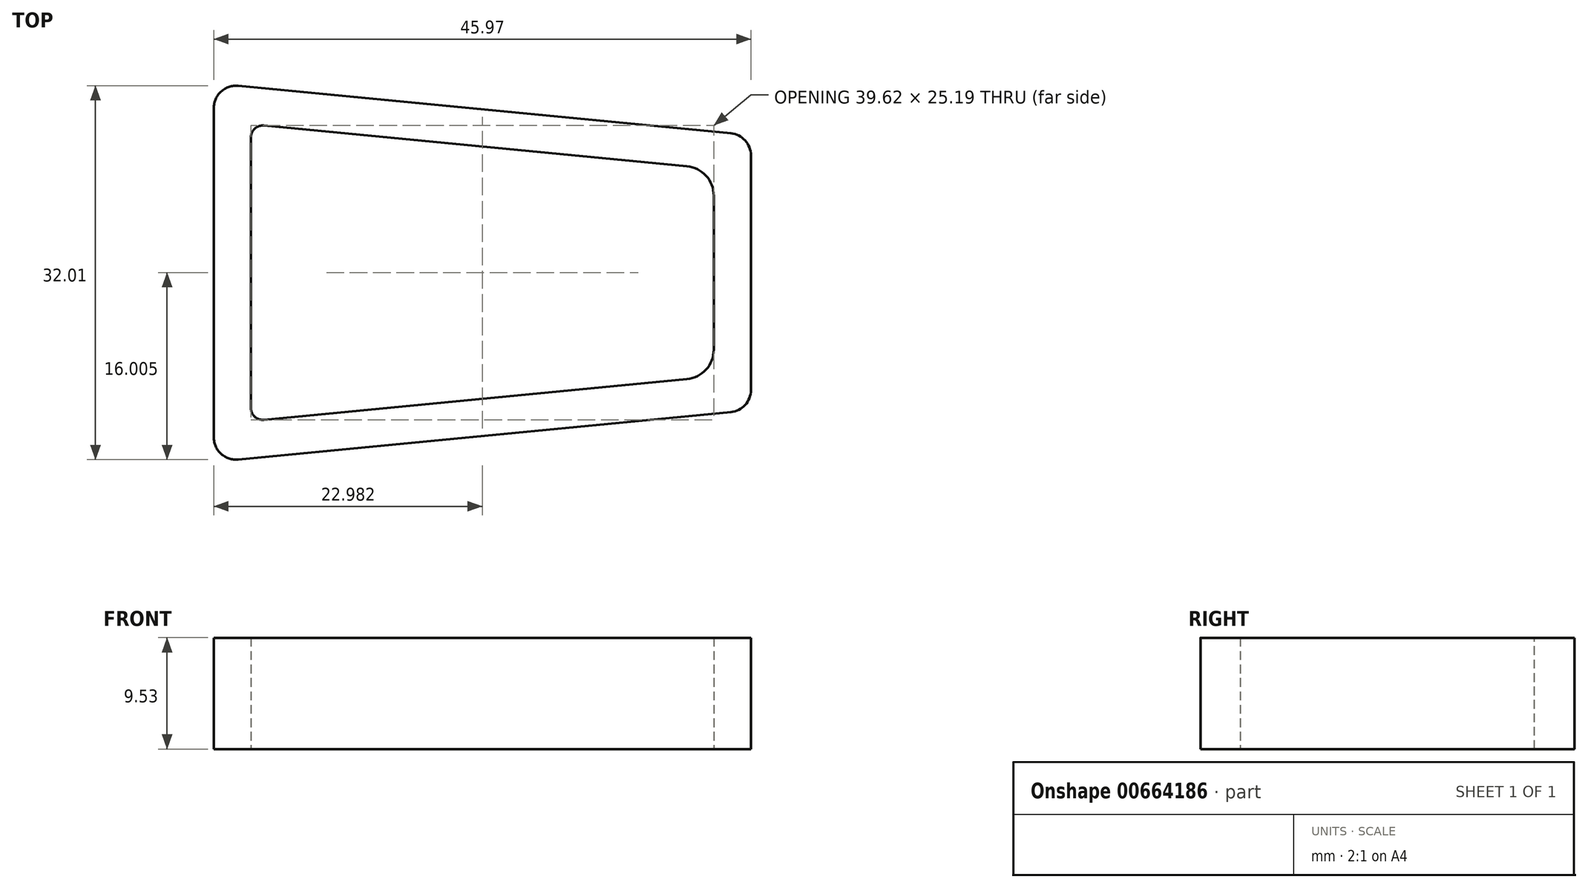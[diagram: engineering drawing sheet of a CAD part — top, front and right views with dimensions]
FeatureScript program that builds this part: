
annotation { "Feature Type Name" : "Feature", "Feature Type Description" : "" }
export const myFeature = defineFeature(function(context is Context, id is Id, definition is map)
    precondition{}
    {
        {
            var Q0;
            Q0=qCreatedBy(makeId("Top.planeOp"),FACE);
            var sketch = newSketch(context, id + "F0", { "sketchPlane" : qUnion([Q0])});
            skLineSegment(sketch, "E0", {"start": v(0, -12.59) * mm, "end": v(0, 12.81) * mm});
            skLineSegment(sketch, "E1", {"start": v(39.62, -8.78) * mm, "end": v(39.62, 9) * mm});
            skPoint(sketch, "E2.endSnap0", {"position": v(0, 0.11) * mm});
            skLineSegment(sketch, "E3", {"start": v(0, 12.81) * mm, "end": v(39.62, 9) * mm});
            skLineSegment(sketch, "E4", {"start": v(0, -12.59) * mm, "end": v(39.62, -8.78) * mm});
            skPoint(sketch, "E2.end.orphan", {"position": v(39.62, 0.11) * mm});
            skLineSegment(sketch, "E5.0", {"start": v(-3.17, -16.08) * mm, "end": v(-3.18, 16.3) * mm});
            skLineSegment(sketch, "E5.1", {"start": v(-3.18, -16.08) * mm, "end": v(42.8, -11.66) * mm});
            skLineSegment(sketch, "E5.2", {"start": v(42.8, -11.66) * mm, "end": v(42.8, 11.89) * mm});
            skLineSegment(sketch, "E5.3", {"start": v(-3.18, 16.3) * mm, "end": v(42.8, 11.89) * mm});
            skSolve(sketch);
        }
        {
            var Q0;
            Q0 = qSketchRegion(id + "F0", true);
            extrude(context, id + "F1", {"entities" : qUnion([Q0]), "depth" : 9.52 * mm, "offsetDistance" : 25.4 * mm});
        }
        {
            var Q0;
            Q0=makeQuery(id+"F1.opExtrude","SWEPT_EDGE",EDGE,{"disambiguationData":[OSD([sQuery(id+"F0.wireOp",EDGE,"E5.1"),sQuery(id+"F0.wireOp",EDGE,"E5.2")])]});
            var Q1;
            Q1=makeQuery(id+"F1.opExtrude","SWEPT_EDGE",EDGE,{"disambiguationData":[OSD([sQuery(id+"F0.wireOp",EDGE,"E5.2"),sQuery(id+"F0.wireOp",EDGE,"E5.3")])]});
            var Q2;
            Q2=makeQuery(id+"F1.opExtrude","SWEPT_EDGE",EDGE,{"disambiguationData":[OSD([sQuery(id+"F0.wireOp",EDGE,"E5.0"),sQuery(id+"F0.wireOp",EDGE,"E5.3")])]});
            var Q3;
            Q3=makeQuery(id+"F1.opExtrude","SWEPT_EDGE",EDGE,{"disambiguationData":[OSD([sQuery(id+"F0.wireOp",EDGE,"E5.0"),sQuery(id+"F0.wireOp",EDGE,"E5.1")])]});
            fillet(context, id + "F2", {"entities" : qUnion([Q0, Q1, Q2, Q3]), "radius" : 1.9 * mm, "tangentPropagation" : true, "allowEdgeOverflow" : false});
        }
        {
            var Q0;
            Q0=makeQuery(id+"F1.opExtrude","SWEPT_EDGE",EDGE,{"disambiguationData":[OSD([sQuery(id+"F0.wireOp",EDGE,"E0"),sQuery(id+"F0.wireOp",EDGE,"E3")])]});
            var Q1;
            Q1=makeQuery(id+"F1.opExtrude","SWEPT_EDGE",EDGE,{"disambiguationData":[OSD([sQuery(id+"F0.wireOp",EDGE,"E0"),sQuery(id+"F0.wireOp",EDGE,"E4")])]});
            fillet(context, id + "F3", {"entities" : qUnion([Q0, Q1]), "radius" : 1.02 * mm, "tangentPropagation" : true, "allowEdgeOverflow" : false});
        }
        {
            var Q0;
            Q0=makeQuery(id+"F1.opExtrude","SWEPT_EDGE",EDGE,{"disambiguationData":[OSD([sQuery(id+"F0.wireOp",EDGE,"E1"),sQuery(id+"F0.wireOp",EDGE,"E3")])]});
            var Q1;
            Q1=makeQuery(id+"F1.opExtrude","SWEPT_EDGE",EDGE,{"disambiguationData":[OSD([sQuery(id+"F0.wireOp",EDGE,"E1"),sQuery(id+"F0.wireOp",EDGE,"E4")])]});
            fillet(context, id + "F4", {"entities" : qUnion([Q0, Q1]), "radius" : 2.54 * mm, "tangentPropagation" : true, "allowEdgeOverflow" : false});
        }
    });
